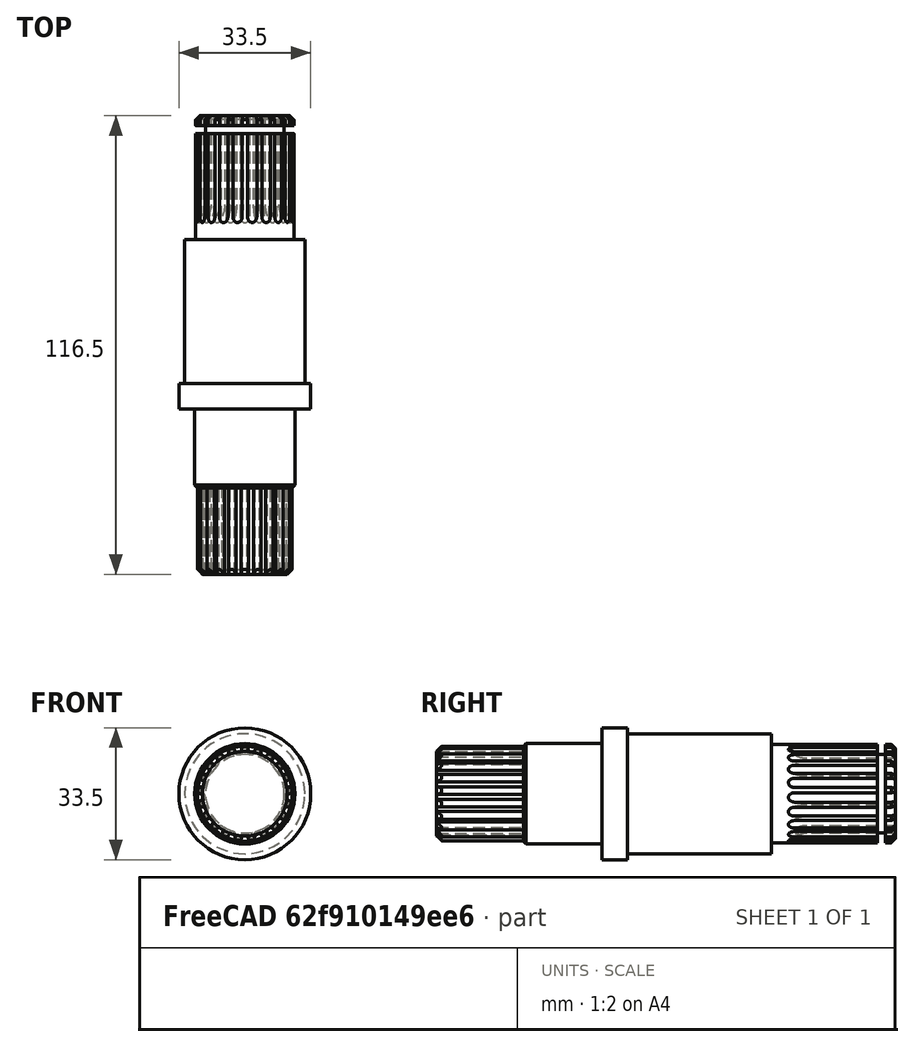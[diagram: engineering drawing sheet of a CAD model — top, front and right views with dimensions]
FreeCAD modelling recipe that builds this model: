
FCSTD DOCUMENT  (FreeCAD 1.0R39319 (Git))
Label: DG_Krushna shaft 
License: All rights reserved
LicenseURL: https://en.wikipedia.org/wiki/All_rights_reserved
objects: Sketcher::SketchObject×12, PartDesign::Pad×6, TechDraw::DrawProjGroupItem×4, PartDesign::PolarPattern×3, PartDesign::Chamfer×3, TechDraw::DrawViewDimension×3, PartDesign::Pocket×1, PartDesign::SubtractivePipe×1, PartDesign::Groove×1, PartDesign::AdditivePipe×1, PartDesign::Fillet×1, PartDesign::Body×1, TechDraw::DrawSVGTemplate×1, TechDraw::DrawProjGroup×1, TechDraw::DrawPage×1
note: 76 computed .brp shape members not serialized (recipe doc carries the construction recipe); baked Part::Feature solids carry a one-line shape summary decoded from their .brp

FEATURE [Sketcher::SketchObject] Sketch
  ArcFitTolerance = 1e-06
  AttachmentSupport = -> [XZ_Plane]
  FullyConstrained = true
  MakeInternals = false
  MapMode = 5
  Placement = pos=(0,0,0) rot=(1,0,0;1.5708rad)
  sketch-geometry (1):
    g0: Circle CenterX=0 CenterY=0 CenterZ=0 NormalX=0 NormalY=0 NormalZ=1 AngleXU=0 Radius=12
  constraints (2):
    c: Diameter(g0) = 24
    c: Coincident(g0,g-1)
FEATURE [PartDesign::Pad] Pad
  Direction = (0,-1,2e-16)
  Length = 22
  Length2 = 10
  Placement = pos=(0,0,0) rot=(1,0,0;1.5708rad)
  Profile = -> Sketch
  ReferenceAxis = -> Sketch [N_Axis]
  Refine = true
  Suppressed = false
  Type = 0
FEATURE [Sketcher::SketchObject] Sketch001
  ArcFitTolerance = 1e-06
  AttachmentSupport = -> [Pad]
  FullyConstrained = true
  MakeInternals = false
  MapMode = 5
  Placement = pos=(0,0,0) rot=(-1,0,0;1.5708rad)
  sketch-geometry (1):
    g0: Circle CenterX=0 CenterY=0 CenterZ=0 NormalX=0 NormalY=0 NormalZ=1 AngleXU=0 Radius=12.75
  constraints (2):
    c: Diameter(g0) = 25.5
    c: Coincident(g0,g-1)
FEATURE [PartDesign::Pad] Pad001
  BaseFeature = -> Pad
  Direction = (0,1,2e-16)
  Length = 20
  Length2 = 10
  Placement = pos=(0,0,0) rot=(1,0,0;1.5708rad)
  Profile = -> Sketch001
  ReferenceAxis = -> Sketch001 [N_Axis]
  Refine = true
  Suppressed = false
  Type = 0
FEATURE [Sketcher::SketchObject] Sketch002
  ArcFitTolerance = 1e-06
  AttachmentSupport = -> [Pad001]
  FullyConstrained = true
  MakeInternals = false
  MapMode = 5
  Placement = pos=(0,20,0) rot=(-1,0,0;1.5708rad)
  sketch-geometry (1):
    g0: Circle CenterX=0 CenterY=0 CenterZ=0 NormalX=0 NormalY=0 NormalZ=1 AngleXU=0 Radius=16.75
  constraints (2):
    c: Diameter(g0) = 33.5
    c: Coincident(g0,g-1)
FEATURE [PartDesign::Pad] Pad002
  BaseFeature = -> Pad001
  Direction = (0,1,2e-16)
  Length = 6.5
  Length2 = 10
  Placement = pos=(0,0,0) rot=(1,0,0;1.5708rad)
  Profile = -> Sketch002
  ReferenceAxis = -> Sketch002 [N_Axis]
  Refine = true
  Suppressed = false
  Type = 0
FEATURE [Sketcher::SketchObject] Sketch003
  ArcFitTolerance = 1e-06
  AttachmentSupport = -> [Pad002]
  FullyConstrained = true
  MakeInternals = false
  MapMode = 5
  Placement = pos=(0,26.5,6.4e-15) rot=(-1,0,0;1.5708rad)
  sketch-geometry (1):
    g0: Circle CenterX=0 CenterY=0 CenterZ=0 NormalX=0 NormalY=0 NormalZ=1 AngleXU=0 Radius=15.25
  constraints (2):
    c: Diameter(g0) = 30.5
    c: Coincident(g0,g-1)
FEATURE [PartDesign::Pad] Pad003
  BaseFeature = -> Pad002
  Direction = (0,1,2e-16)
  Length = 36.5
  Length2 = 10
  Placement = pos=(0,0,0) rot=(1,0,0;1.5708rad)
  Profile = -> Sketch003
  ReferenceAxis = -> Sketch003 [N_Axis]
  Refine = true
  Suppressed = false
  Type = 0
FEATURE [Sketcher::SketchObject] Sketch004
  ArcFitTolerance = 1e-06
  AttachmentSupport = -> [Pad003]
  ExternalGeometry = -> [Pad003]
  FullyConstrained = true
  MakeInternals = false
  MapMode = 5
  Placement = pos=(0,63,1.7e-14) rot=(-1,0,0;1.5708rad)
  sketch-geometry (1):
    g0: Circle CenterX=0 CenterY=0 CenterZ=0 NormalX=0 NormalY=0 NormalZ=1 AngleXU=0 Radius=12.5
  constraints (2):
    c: Coincident(g0,g-1)
    c: Distance(g0,g-3) = 2.75
FEATURE [PartDesign::Pad] Pad004
  BaseFeature = -> Pad003
  Direction = (0,1,2e-16)
  Length = 7
  Length2 = 10
  Placement = pos=(0,0,0) rot=(1,0,0;1.5708rad)
  Profile = -> Sketch004
  ReferenceAxis = -> Sketch004 [N_Axis]
  Refine = true
  Suppressed = false
  Type = 0
FEATURE [Sketcher::SketchObject] Sketch005
  ArcFitTolerance = 1e-06
  AttachmentSupport = -> [Pad004]
  ExternalGeometry = -> [Pad004]
  FullyConstrained = true
  MakeInternals = false
  MapMode = 5
  Placement = pos=(0,70,0) rot=(-1,0,0;1.5708rad)
  sketch-geometry (2):
    g0: Circle CenterX=0 CenterY=0 CenterZ=0 NormalX=0 NormalY=0 NormalZ=1 AngleXU=0 Radius=12.5
    g1: GeomPoint X=0 Y=12.5 Z=0
  constraints (4):
    c: Coincident(g0,g-1)
    c: PointOnObject(g1,g-3)
    c: PointOnObject(g1,g-2)
    c: PointOnObject(g1,g0)
FEATURE [PartDesign::Pad] Pad005
  BaseFeature = -> Pad004
  Direction = (0,1,2e-16)
  Length = 24.5
  Length2 = 10
  Placement = pos=(0,0,0) rot=(1,0,0;1.5708rad)
  Profile = -> Sketch005
  ReferenceAxis = -> Sketch005 [N_Axis]
  Refine = true
  Suppressed = false
  Type = 0
FEATURE [Sketcher::SketchObject] Sketch006
  ArcFitTolerance = 1e-06
  AttachmentSupport = -> [Pad005]
  ExternalGeometry = -> [Pad005]
  FullyConstrained = true
  MakeInternals = false
  MapMode = 5
  Placement = pos=(0,-22,0) rot=(1,0,0;1.5708rad)
  sketch-geometry (2):
    g0: Circle CenterX=0 CenterY=0 CenterZ=0 NormalX=0 NormalY=0 NormalZ=1 AngleXU=0 Radius=10.75
    g1: Circle CenterX=0 CenterY=0 CenterZ=0 NormalX=0 NormalY=0 NormalZ=1 AngleXU=0 Radius=13.815
  constraints (4):
    c: Coincident(g0,g-1)
    c: Distance(g-3,g0) = 1.25
    c: Coincident(g1,g0)
    c: Diameter(g1) = 27.63
FEATURE [PartDesign::Pocket] Pocket
  BaseFeature = -> Pad005
  Direction = (0,1,-2e-16)
  Length = 22
  Length2 = 5
  Placement = pos=(0,0,0) rot=(1,0,0;1.5708rad)
  Profile = -> Sketch006
  ReferenceAxis = -> Sketch006 [N_Axis]
  Refine = true
  Suppressed = false
  Type = 0
FEATURE [PartDesign::PolarPattern] PolarPattern
  Angle = 360
  Axis = -> Sketch006 [N_Axis]
  BaseFeature = -> Pocket
  Mode = 0
  Occurrences = 21
  Offset = 120
  Originals = -> [Pocket]
  Placement = pos=(0,0,0) rot=(1,0,0;1.5708rad)
  Refine = true
  Suppressed = false
  TransformMode = 0
FEATURE [Sketcher::SketchObject] Sketch007
  ArcFitTolerance = 1e-06
  AttachmentSupport = -> [PolarPattern]
  ExternalGeometry = -> [PolarPattern]
  FullyConstrained = true
  MakeInternals = false
  MapMode = 5
  Placement = pos=(0,94.5,0) rot=(-1,0,0;1.5708rad)
  sketch-geometry (6):
    g0: ArcOfCircle CenterX=0 CenterY=13.71 CenterZ=0 NormalX=0 NormalY=0 NormalZ=1 AngleXU=0 Radius=1.21 StartAngle=-9e-16 EndAngle=3.14159
    g1: ArcOfCircle CenterX=1e-16 CenterY=11.29 CenterZ=0 NormalX=0 NormalY=0 NormalZ=1 AngleXU=0 Radius=1.21 StartAngle=3.14159 EndAngle=6.28319
    g2: LineSegment StartX=1.21 StartY=13.71 StartZ=0 EndX=1.21 EndY=11.29 EndZ=0
    g3: LineSegment StartX=-1.21 StartY=13.71 StartZ=0 EndX=-1.21 EndY=11.29 EndZ=0
    g4: LineSegment [constr] StartX=0 StartY=13.71 StartZ=0 EndX=1e-16 EndY=11.29 EndZ=0
    g5: GeomPoint [constr] X=0 Y=12.5 Z=0
  constraints (13):
    c: Tangent(g0,g2) = 1.5708
    c: Tangent(g0,g3) = -1.5708
    c: Tangent(g1,g2) = 1.5708
    c: Tangent(g1,g3) = -1.5708
    c: Equal(g0,g1)
    c: PointOnObject(g0,g-2)
    c: Vertical(g2)
    c: Distance(g2,g3) = 2.42
    c: DistanceY(g1,g0) = 2.42
    c: Coincident(g4,g0)
    c: Coincident(g4,g1)
    c: Symmetric(g4,g4,g5)
    c: PointOnObject(g5,g-3)
FEATURE [Sketcher::SketchObject] Sketch008
  ArcFitTolerance = 1e-06
  AttachmentSupport = -> [YZ_Plane]
  ExternalGeometry = -> [PolarPattern]
  FullyConstrained = true
  MakeInternals = false
  MapMode = 5
  Placement = pos=(0,0,0) rot=(0.57735,0.57735,0.57735;2.0944rad)
  sketch-geometry (2):
    g0: LineSegment StartX=94.5 StartY=-12.5 StartZ=0 EndX=72 EndY=-12.5 EndZ=0
    g1: ArcOfCircle CenterX=72 CenterY=-15.75 CenterZ=0 NormalX=0 NormalY=0 NormalZ=1 AngleXU=0 Radius=3.25 StartAngle=1.5708 EndAngle=2.98713
  constraints (6):
    c: Horizontal(g0)
    c: Tangent(g0,g1) = -1.5708
    c: Radius(g1) = 3.25
    c: DistanceX(g0,g0) = 22.5
    c: Coincident(g0,g-3)
    c: Horizontal(g1,g-4)
FEATURE [PartDesign::SubtractivePipe] SubtractivePipe
  AuxilleryCurvelinear = true
  AuxillerySpineTangent = false
  BaseFeature = -> PolarPattern
  Binormal = (0,0,0)
  Mode = 0
  Placement = pos=(0,0,0) rot=(1,0,0;1.5708rad)
  Profile = -> Sketch007
  Refine = true
  Spine = -> Sketch008
  SpineTangent = false
  Suppressed = false
  Transformation = 0
  Transition = 0
FEATURE [PartDesign::PolarPattern] PolarPattern001
  Angle = 360
  Axis = -> Sketch007 [N_Axis]
  BaseFeature = -> SubtractivePipe
  Mode = 0
  Occurrences = 21
  Offset = 120
  Originals = -> [SubtractivePipe]
  Placement = pos=(0,0,0) rot=(1,0,0;1.5708rad)
  Refine = true
  Suppressed = false
  TransformMode = 0
FEATURE [PartDesign::Chamfer] Chamfer
  Angle = 45
  Base = -> PolarPattern001 [Edge124,Edge128,Edge136,Edge56,Edge132,Edge60,Edge64,Edge68,Edge72,Edge76,Edge80,Edge84,Edge88,Edge92,Edge96,Edge100,Edge104,Edge108,Edge112,Edge116,Edge120]
  BaseFeature = -> PolarPattern001
  ChamferType = 0
  FlipDirection = false
  Placement = pos=(0,0,0) rot=(1,0,0;1.5708rad)
  Refine = true
  Size = 1
  Size2 = 1
  SupportTransform = false
  Suppressed = false
  UseAllEdges = false
FEATURE [Sketcher::SketchObject] Sketch011
  ArcFitTolerance = 1e-06
  AttachmentSupport = -> [YZ_Plane]
  ExternalGeometry = -> [Chamfer]
  FullyConstrained = true
  MakeInternals = false
  MapMode = 5
  Placement = pos=(0,0,0) rot=(0.57735,0.57735,0.57735;2.0944rad)
  sketch-geometry (4):
    g0: LineSegment StartX=92 StartY=9.98268 StartZ=0 EndX=92 EndY=12.9827 EndZ=0
    g1: LineSegment StartX=90 StartY=12.9827 StartZ=0 EndX=90 EndY=9.98268 EndZ=0
    g2: LineSegment StartX=90 StartY=9.98268 StartZ=0 EndX=92 EndY=9.98268 EndZ=0
    g3: LineSegment StartX=90 StartY=12.9827 StartZ=0 EndX=92 EndY=12.9827 EndZ=0
  constraints (12):
    c: Coincident(g1,g2)
    c: Coincident(g2,g0)
    c: Vertical(g0)
    c: Vertical(g1)
    c: Horizontal(g2)
    c: Distance(g0,g1) = 2
    c: Distance(g-3,g0) = 2.5
    c: Distance(g2,g-4) = 2.5
    c: Coincident(g3,g1)
    c: Coincident(g3,g0)
    c: Horizontal(g3)
    c: Distance(g0,g0) = 3
FEATURE [PartDesign::Groove] Groove
  Angle = 360
  Angle2 = 60
  Axis = (1e-16,1,-1e-16)
  Base = (0,0,0)
  BaseFeature = -> Chamfer
  Placement = pos=(0,0,0) rot=(1,0,0;1.5708rad)
  Profile = -> Sketch011
  ReferenceAxis = -> Y_Axis
  Refine = true
  Reversed = true
  Suppressed = false
  Type = 0
FEATURE [Sketcher::SketchObject] Sketch012
  ArcFitTolerance = 1e-06
  AttachmentSupport = -> [Groove]
  ExternalGeometry = -> [Groove]
  FullyConstrained = true
  MakeInternals = false
  MapMode = 5
  Placement = pos=(0,-22,0) rot=(1,0,0;1.5708rad)
  sketch-geometry (6):
    g0: LineSegment StartX=-0.988345 StartY=10.7045 StartZ=0 EndX=-0.67 EndY=11.9813 EndZ=0
    g1: LineSegment StartX=0.67 StartY=11.9813 StartZ=0 EndX=0.988345 EndY=10.7045 EndZ=0
    g2: ArcOfCircle CenterX=0 CenterY=0 CenterZ=0 NormalX=0 NormalY=0 NormalZ=1 AngleXU=0 Radius=10.75 StartAngle=1.47873 EndAngle=1.66287
    g3: ArcOfCircle CenterX=0 CenterY=0 CenterZ=0 NormalX=0 NormalY=0 NormalZ=1 AngleXU=0 Radius=12 StartAngle=1.51493 EndAngle=1.62666
    g4: LineSegment [constr] StartX=-2.2602 StartY=13.7367 StartZ=0 EndX=-2.2602 EndY=8.16723 EndZ=0
    g5: LineSegment [constr] StartX=4.20492 StartY=13.7481 StartZ=0 EndX=4.20492 EndY=8.1902 EndZ=0
  constraints (16):
    c: PointOnObject(g0,g-3)
    c: Equal(g0,g1)
    c: Coincident(g2,g-1)
    c: Coincident(g2,g0)
    c: Coincident(g2,g1)
    c: Radius(g3) = 12
    c: Coincident(g3,g2)
    c: Coincident(g3,g0)
    c: Coincident(g3,g1)
    c: Vertical(g4)
    c: Vertical(g5)
    c: Block(g4)
    c: Block(g5)
    c: Angle(g0,g4) = 0.244346
    c: Angle(g5,g1) = 0.244346
    c: DistanceX(g0,g1) = 1.34
FEATURE [Sketcher::SketchObject] Sketch013
  ArcFitTolerance = 1e-06
  AttachmentSupport = -> [YZ_Plane]
  ExternalGeometry = -> [Groove]
  FullyConstrained = true
  MakeInternals = false
  MapMode = 5
  Placement = pos=(0,0,0) rot=(0.57735,0.57735,0.57735;2.0944rad)
  sketch-geometry (1):
    g0: LineSegment StartX=-22 StartY=10.75 StartZ=0 EndX=3.6e-15 EndY=10.75 EndZ=0
  constraints (3):
    c: Horizontal(g0)
    c: Coincident(g0,g-3)
    c: DistanceX(g0,g0) = 22
FEATURE [PartDesign::AdditivePipe] AdditivePipe
  AuxilleryCurvelinear = true
  AuxillerySpineTangent = false
  BaseFeature = -> Groove
  Binormal = (0,0,0)
  Mode = 0
  Placement = pos=(0,0,0) rot=(1,0,0;1.5708rad)
  Profile = -> Sketch012
  Refine = true
  Spine = -> Sketch013
  SpineTangent = false
  Suppressed = false
  Transformation = 0
  Transition = 0
FEATURE [PartDesign::PolarPattern] PolarPattern002
  Angle = 360
  Axis = -> Sketch012 [N_Axis]
  BaseFeature = -> AdditivePipe
  Mode = 0
  Occurrences = 21
  Offset = 120
  Originals = -> [AdditivePipe]
  Placement = pos=(0,0,0) rot=(1,0,0;1.5708rad)
  Refine = true
  Suppressed = false
  TransformMode = 0
FEATURE [PartDesign::Chamfer] Chamfer001
  Angle = 45
  Base = -> PolarPattern002 [Edge582]
  BaseFeature = -> PolarPattern002
  ChamferType = 0
  FlipDirection = false
  Placement = pos=(0,0,0) rot=(1,0,0;1.5708rad)
  Refine = true
  Size = 0.71
  Size2 = 1
  SupportTransform = false
  Suppressed = false
  UseAllEdges = false
FEATURE [PartDesign::Chamfer] Chamfer002
  Angle = 45
  Base = -> Chamfer001 [Edge107,Edge99,Edge259,Edge251,Edge115,Edge243,Edge235,Edge227,Edge219,Edge211,Edge203,Edge195,Edge187,Edge179,Edge171,Edge163,Edge155,Edge147,Edge139,Edge131,Edge123]
  BaseFeature = -> Chamfer001
  ChamferType = 0
  FlipDirection = false
  Placement = pos=(0,0,0) rot=(1,0,0;1.5708rad)
  Refine = true
  Size = 1.25
  Size2 = 1
  SupportTransform = false
  Suppressed = false
  UseAllEdges = false
FEATURE [PartDesign::Fillet] Fillet
  Base = -> Chamfer002 [Edge225,Edge223,Edge218,Edge216,Edge230,Edge232,Edge237,Edge239,Edge244,Edge246,Edge211,Edge209,Edge204,Edge202,Edge197,Edge253,Edge190,Edge188,Edge183,Edge181,Edge176,Edge174,Edge169,Edge167,Edge162,Edge160,Edge155,Edge153,Edge148,Edge146,Edge141,Edge139,Edge5,Edge1,Edge274,Edge272,Edge267,Edge265,Edge260,Edge258,+1 more]
  BaseFeature = -> Chamfer002
  Placement = pos=(0,0,0) rot=(1,0,0;1.5708rad)
  Radius = 0.5
  Refine = true
  SupportTransform = false
  Suppressed = false
  UseAllEdges = false
FEATURE [PartDesign::Body] Body  label="shaft"
  AllowCompound = false
  Group = -> [Sketch,Pad,Sketch001,Pad001,Sketch002,Pad002,Sketch003,Pad003,Sketch004,Pad004,Sketch005,Pad005,Sketch006,Pocket,PolarPattern,Sketch007,Sketch008,SubtractivePipe,PolarPattern001,Chamfer,Sketch011,Groove,Sketch012,Sketch013,AdditivePipe,PolarPattern002,Chamfer001,Chamfer002,Fillet]
  Origin = -> Origin
  Tip = -> Fillet
FEATURE [TechDraw::DrawSVGTemplate] Template
  EditableTexts = AuthorName=Krushna manwatkar; CheckDate=CHECK DATE; CreationDate=06-01-2026; DrawingNumber=NUMBER; FC-Title=DG_Krushna shaft; SheetNumber=1 / 1; Subtitle=SUBTITLE; SupervisorName=SUPERVISOR NAME; Weight=WEIGHT; scale=1 : 1
  Height = 297
  Orientation = 1
  Template = C:/Program Files/FreeCAD 1.0/data/Mod/TechDraw/Templates/A3_Landscape_TD.svg
  Width = 420
FEATURE [TechDraw::DrawProjGroupItem] View  label="Front"
  CoarseView = false
  Direction = (0,-1,0)
  Focus = 100
  HardHidden = false
  IsoCount = 0
  IsoHidden = false
  IsoVisible = false
  LockPosition = true
  Perspective = false
  Rotation = 0
  RotationVector = (1,0,0)
  ScaleType = 2
  ScrubCount = 1
  SeamHidden = false
  SeamVisible = false
  SmoothHidden = false
  SmoothVisible = true
  Source = -> [Body]
  Type = 0
  X = 0
  XDirection = (1,0,0)
  Y = 0
FEATURE [TechDraw::DrawProjGroupItem] ProjItem  label="Bottom"
  CoarseView = false
  Direction = (0,0,-1)
  Focus = 100
  HardHidden = false
  IsoCount = 0
  IsoHidden = false
  IsoVisible = false
  LockPosition = false
  Perspective = false
  Rotation = 0
  RotationVector = (1,0,0)
  ScaleType = 0
  ScrubCount = 1
  SeamHidden = false
  SeamVisible = false
  SmoothHidden = false
  SmoothVisible = true
  Source = -> [Body]
  Type = 5
  X = 0
  XDirection = (1,0,0)
  Y = 90
FEATURE [TechDraw::DrawProjGroupItem] ProjItem001  label="Left"
  CoarseView = false
  Direction = (-1,-1e-16,0)
  Focus = 100
  HardHidden = false
  IsoCount = 0
  IsoHidden = false
  IsoVisible = false
  LockPosition = false
  Perspective = false
  Rotation = 0
  RotationVector = (1,0,0)
  ScaleType = 0
  ScrubCount = 1
  SeamHidden = false
  SeamVisible = false
  SmoothHidden = false
  SmoothVisible = true
  Source = -> [Body]
  Type = 1
  X = 90
  XDirection = (1e-16,-1,0)
  Y = 0
FEATURE [TechDraw::DrawProjGroupItem] ProjItem002  label="FrontBottomLeft"
  CoarseView = false
  Direction = (-0.57735,-0.57735,-0.57735)
  Focus = 100
  HardHidden = false
  IsoCount = 0
  IsoHidden = false
  IsoVisible = false
  LockPosition = false
  Perspective = false
  Rotation = 0
  RotationVector = (1,0,0)
  ScaleType = 0
  ScrubCount = 1
  SeamHidden = false
  SeamVisible = false
  SmoothHidden = false
  SmoothVisible = true
  Source = -> [Body]
  Type = 8
  X = 90
  XDirection = (0.707107,-0.707107,0)
  Y = 90
FEATURE [TechDraw::DrawProjGroup] ProjGroup
  Anchor = -> View
  AutoDistribute = true
  LockPosition = false
  ProjectionType = 0
  Rotation = 0
  ScaleType = 0
  Source = -> [Body]
  Views = -> [View,ProjItem,ProjItem001,ProjItem002]
  X = 74.7037
  Y = 105.748
  spacingX = 15
  spacingY = 15
FEATURE [TechDraw::DrawViewDimension] Dimension
  AngleOverride = false
  Arbitrary = false
  ArbitraryTolerances = false
  BoxCorners = (2) [(-16.75,-58.25,-1e-07),(16.75,58.25,1e-07)]
  EqualTolerance = true
  ExtensionAngle = 0
  FormatSpec = %.2w
  FormatSpecOverTolerance = %+.2w
  FormatSpecUnderTolerance = %+.2w
  Inverted = false
  LineAngle = 0
  LockPosition = false
  MeasureType = 1
  OverTolerance = 0
  References2D = -> [ProjItem]
  Rotation = 0
  ScaleType = 0
  TheoreticalExact = false
  Type = 2
  UnderTolerance = 0
  X = -54.0353
  Y = -0.434121
FEATURE [TechDraw::DrawViewDimension] Dimension001
  AngleOverride = false
  Arbitrary = false
  ArbitraryTolerances = false
  BoxCorners = (2) [(-16.75,-58.25,-1e-07),(16.75,58.25,1e-07)]
  EqualTolerance = true
  ExtensionAngle = 0
  FormatSpec = %.2w
  FormatSpecOverTolerance = %+.2w
  FormatSpecUnderTolerance = %+.2w
  Inverted = false
  LineAngle = 0
  LockPosition = false
  MeasureType = 1
  OverTolerance = 0
  References2D = -> [ProjItem]
  Rotation = 0
  ScaleType = 0
  TheoreticalExact = false
  Type = 0
  UnderTolerance = 0
  X = 61.6414
  Y = 52.6573
FEATURE [TechDraw::DrawViewDimension] Dimension002
  AngleOverride = false
  Arbitrary = false
  ArbitraryTolerances = false
  BoxCorners = (2) [(-16.75,-16.75,-1e-07),(16.75,16.75,1e-07)]
  EqualTolerance = true
  ExtensionAngle = 0
  FormatSpec = ⌀%.2w
  FormatSpecOverTolerance = %+.2w
  FormatSpecUnderTolerance = %+.2w
  Inverted = false
  LineAngle = 0
  LockPosition = false
  MeasureType = 1
  OverTolerance = 0
  References2D = -> [View]
  Rotation = 0
  ScaleType = 0
  TheoreticalExact = false
  Type = 5
  UnderTolerance = 0
  X = -29.2868
  Y = 2.70863
FEATURE [TechDraw::DrawPage] Page
  KeepUpdated = true
  NextBalloonIndex = 1
  ProjectionType = 0
  Template = -> Template
  Views = -> [ProjGroup,Dimension,Dimension001,Dimension002]
